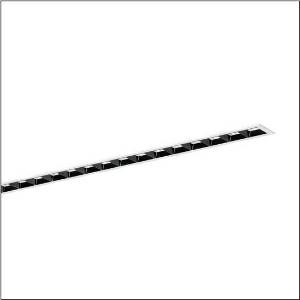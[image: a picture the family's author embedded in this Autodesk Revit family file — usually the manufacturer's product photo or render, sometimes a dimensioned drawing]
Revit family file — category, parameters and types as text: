
# Revit family: silica_21_51mx12da34wb
name_source: partatom
category: Lighting Fixtures
units: mm (PartAtom-declared; Revit-internal decimal feet)

## family parameters
Cut with Voids When Loaded = No
Host = Face
Light Source = No
Part Type = Normal
Room Calculation Point = No
Round Connector Dimension = Use Diameter
Shared = No

## types (1)
- --- (1 x LED, 4320 lm, 27.4 W, 3000K)
    Apparent Load = 27 VA
    CIE Flux Codes = 86 100 100 100 100
    Color Rendering = 80
    Color Temperature = 3000K
    Default Elevation = 1800 mm
    Description = Silica 21, office luminaire, primary light control with darklight reflector, of PMMA, black, CAT 2 (L<= 3000cd/m²), light emission: direct distribution, primary light characteristic: symmetric, installation type: recessed, LED, rated luminous flux: 4.320lm, luminous efficacy: 158lm/W, light colour: 830, colour temperature: 3000K, control gear: DALI 2, with terminal, 3+2-pole, max. 2.5mm², mains connection: 220..240V, AC, 50/60Hz, rated input power: 27.4W, luminaire housing, of aluminium, traffic white (RAL 9016), length: 1.228mm, width: 79mm, height: 53mm, protection rating (complete): IP20, insulation class (complete): insulation class I (protective earthing), certification: CE, ENEC, VDE, permissible operating ambient temperature: 0..+35°C, standard: EN 50419, packaging unit: 1 piece
    Height = 0 mm  [stored 0 ft]
    Lamp = 1 x LED
    Lamp Light Flux = 4320 lm
    Lamp Power = 27.4 W
    Lamp count = 1
    Length = 1227 mm
    Luminous efficacy = 158 lm/W
    Manufacturer = Siteco
    ModVariant = No
    Model = 51MX12DA34WB
    Mounting Place = Ceiling
    Mounting Type = Recessed
    Number of Poles = 1
    OnlyDefault = Yes
    Power Factor = 1
    Product Name = Silica 21
    Product group = office luminaire | ceiling recessed
    ProductGroupID = 400
    Protection Class = Protection class I
    Protection Degree = IP 20
    RLX_Detail_Level = 1
    RLX_Emergency_Light_Flux = 0 lm
    RLX_Emergency_Type = 0
    RLX_Emergency_Type_DB = No
    RlxData = <blob elided: 38857 chars, md5=6360fc04>
    Socket = socket
    Standby Power = 0 W
    System Light Flux = 4320 lm
    System Power = 27 W
    Type Comments = factory setting: luminous flux: 100 % | dim-lin: 254 | 392 mA
    Type Image = l_1335880.jpg
    URL = http://relux.com
    VarID = @adj_028833
    Voltage = 0 V
    Weight = 0.00 kg
    Width = 79 mm

note: [stored X ft] marks values corroborated as IEEE doubles in the binary element streams (Revit-internal decimal feet)

## geometry (parser evidence)
native form markers: Blend x4, Sweep x10
no freeform markers — native parametric forms only
